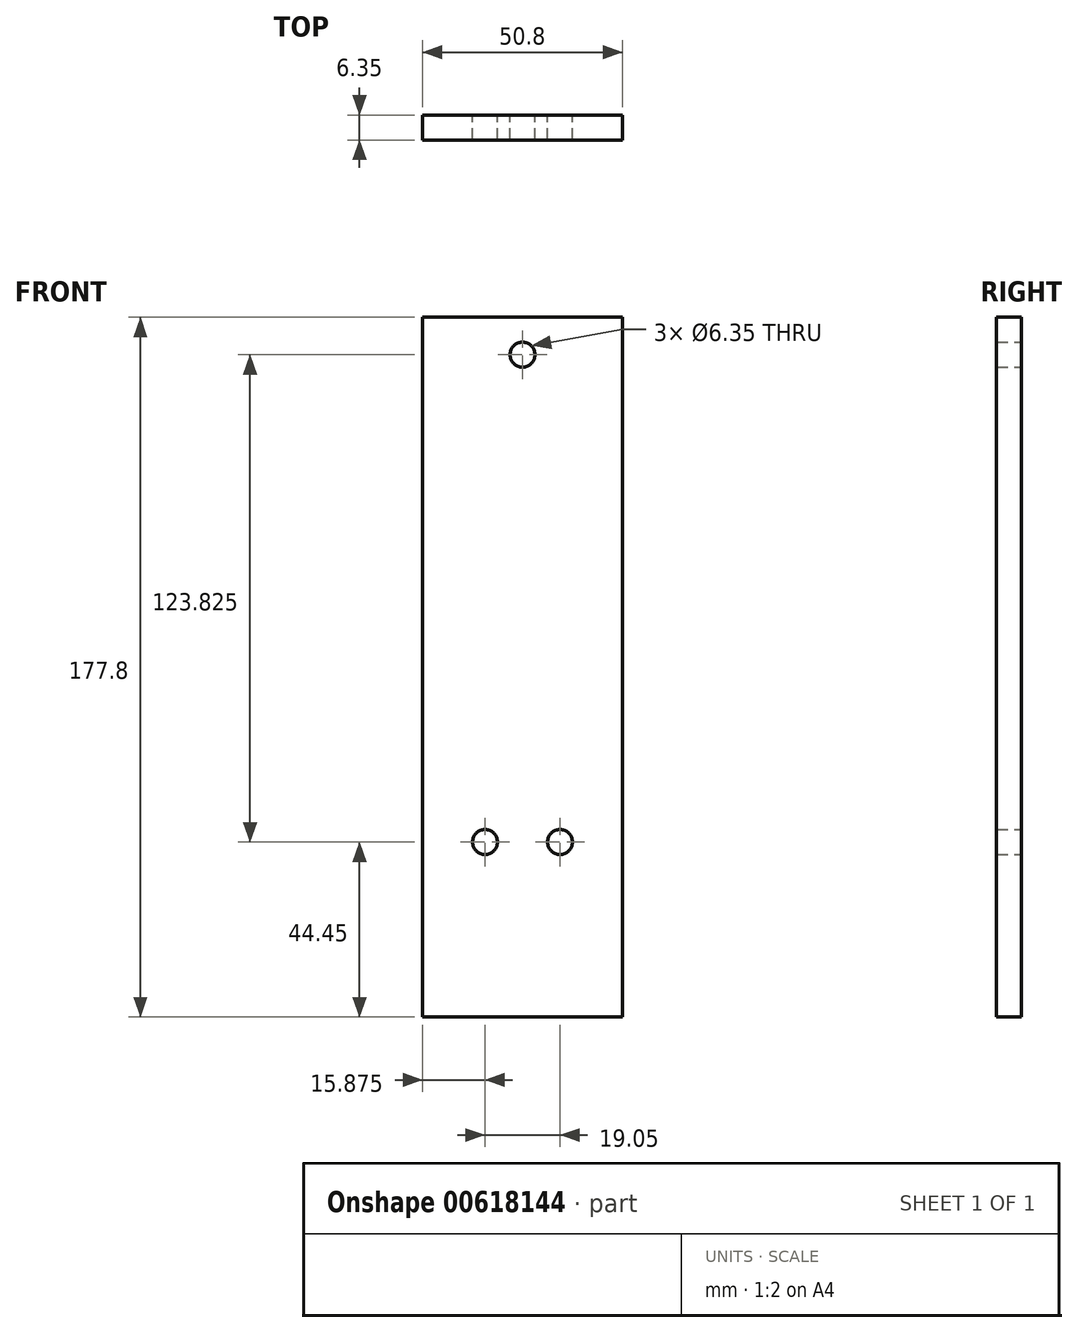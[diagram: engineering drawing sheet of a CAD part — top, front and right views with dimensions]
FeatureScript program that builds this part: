
annotation { "Feature Type Name" : "Feature", "Feature Type Description" : "" }
export const myFeature = defineFeature(function(context is Context, id is Id, definition is map)
    precondition{}
    {
        {
            var Q0;
            Q0=qCreatedBy(makeId("Front.planeOp"),FACE);
            var sketch = newSketch(context, id + "F0", { "sketchPlane" : qUnion([Q0])});
            skLineSegment(sketch, "E0.bottom", {"start": v(0, 0) * mm, "end": v(50.8, 0) * mm});
            skLineSegment(sketch, "E0.top", {"start": v(0, 177.8) * mm, "end": v(50.8, 177.8) * mm});
            skLineSegment(sketch, "E0.left", {"start": v(0, 0) * mm, "end": v(0, 177.8) * mm});
            skLineSegment(sketch, "E0.right", {"start": v(50.8, 0) * mm, "end": v(50.8, 177.8) * mm});
            skLineSegment(sketch, "E1", {"start": v(25.4, 177.8) * mm, "end": v(25.4, 44.45) * mm});
            skLineSegment(sketch, "E2", {"start": v(15.87, 44.45) * mm, "end": v(34.93, 44.45) * mm});
            skCircle(sketch, "E3", {"center": v(34.93, 44.45) * mm, "radius": 3.18 * mm});
            skCircle(sketch, "E4", {"center": v(15.87, 44.45) * mm, "radius": 3.18 * mm});
            skCircle(sketch, "E5", {"center": v(25.4, 168.28) * mm, "radius": 3.18 * mm});
            skSolve(sketch);
        }
        {
            var Q0;
            Q0=qSketchRegion(id+"F0",true);
            extrude(context, id + "F1", {"entities" : qUnion([Q0]), "depth" : 6.35 * mm});
        }
    });
